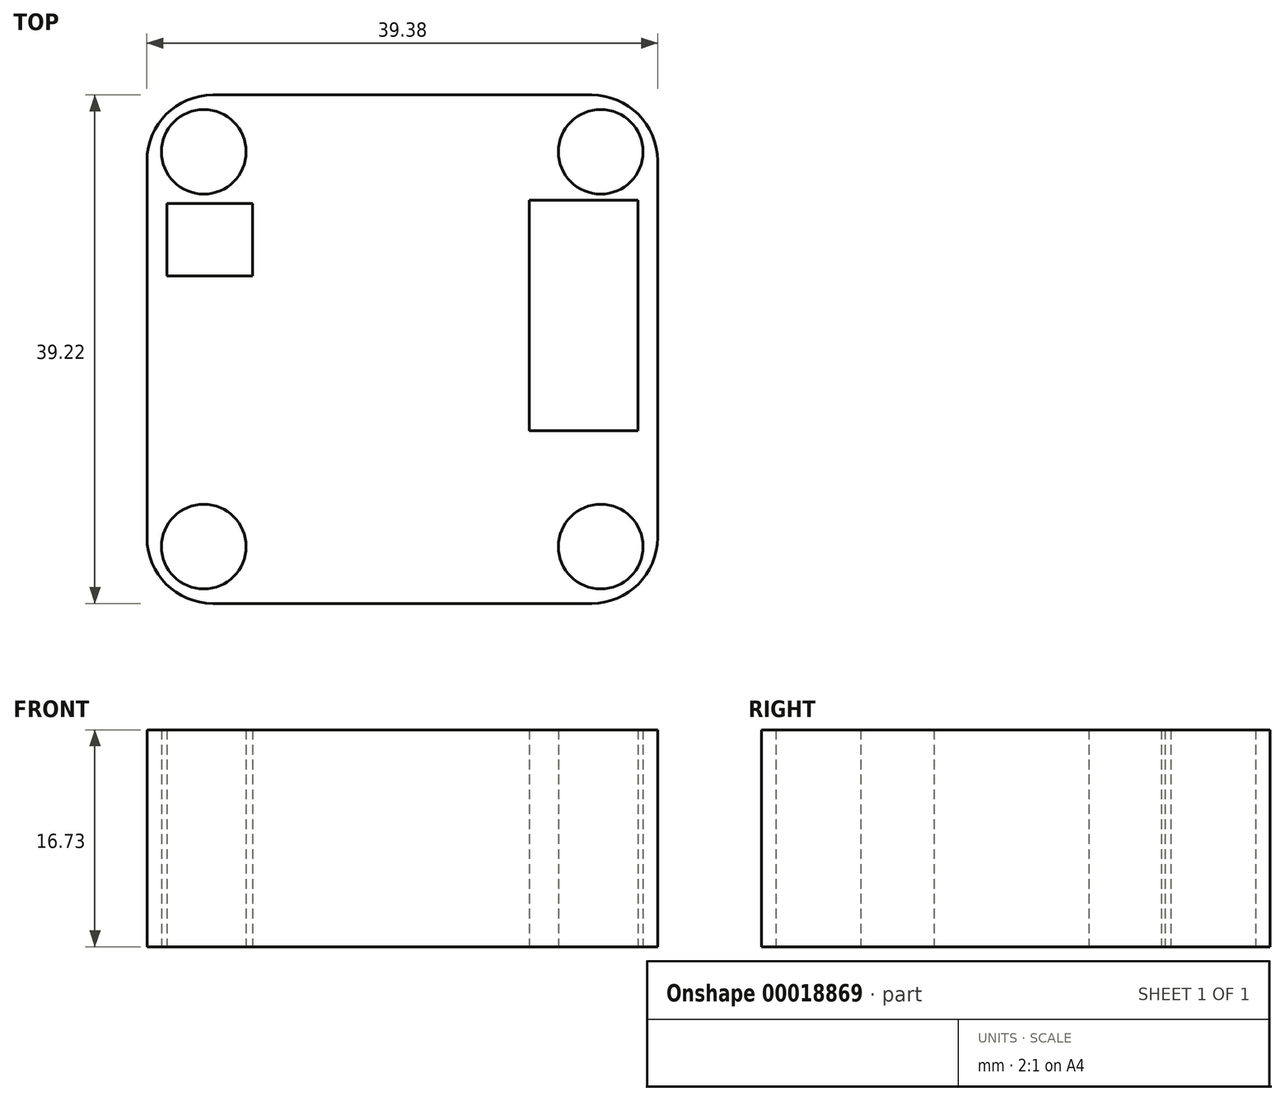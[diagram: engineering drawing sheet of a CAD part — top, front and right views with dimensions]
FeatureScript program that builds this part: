
annotation { "Feature Type Name" : "Feature", "Feature Type Description" : "" }
export const myFeature = defineFeature(function(context is Context, id is Id, definition is map)
    precondition{}
    {
        {
            var Q0;
            Q0=qCreatedBy(makeId("Top.planeOp"),FACE);
            var sketch = newSketch(context, id + "F0", { "sketchPlane" : qUnion([Q0])});
            skLineSegment(sketch, "E0.rect.bottom", {"start": v(19.69, -19.6) * mm, "end": v(-19.69, -19.6) * mm});
            skLineSegment(sketch, "E0.rect.top", {"start": v(19.69, 19.6) * mm, "end": v(-19.69, 19.6) * mm});
            skLineSegment(sketch, "E0.rect.left", {"start": v(19.69, -19.6) * mm, "end": v(19.69, 19.6) * mm});
            skLineSegment(sketch, "E0.rect.right", {"start": v(-19.69, -19.6) * mm, "end": v(-19.69, 19.6) * mm});
            skPoint(sketch, "E0.rect.middle", {"position": v(0, 0) * mm});
            skLineSegment(sketch, "E1.bottom", {"start": v(9.78, 11.5) * mm, "end": v(18.19, 11.5) * mm});
            skLineSegment(sketch, "E1.top", {"start": v(9.78, -6.3) * mm, "end": v(18.19, -6.3) * mm});
            skLineSegment(sketch, "E1.left", {"start": v(9.78, 11.5) * mm, "end": v(9.78, -6.3) * mm});
            skLineSegment(sketch, "E1.right", {"start": v(18.19, 11.5) * mm, "end": v(18.19, -6.3) * mm});
            skLineSegment(sketch, "E2.bottom", {"start": v(-18.16, 11.23) * mm, "end": v(-11.56, 11.23) * mm});
            skLineSegment(sketch, "E2.top", {"start": v(-18.16, 5.64) * mm, "end": v(-11.56, 5.64) * mm});
            skLineSegment(sketch, "E2.left", {"start": v(-18.16, 11.23) * mm, "end": v(-18.16, 5.64) * mm});
            skLineSegment(sketch, "E2.right", {"start": v(-11.56, 11.23) * mm, "end": v(-11.56, 5.64) * mm});
            skCircle(sketch, "E3", {"center": v(-15.3, -15.23) * mm, "radius": 3.26 * mm});
            skLineSegment(sketch, "E4", {"start": v(0, 0) * mm, "end": v(0, -19.6) * mm, "construction": true});
            skCircle(sketch, "E5.MirrorC", {"center": v(15.3, -15.23) * mm, "radius": 3.26 * mm});
            skLineSegment(sketch, "E6", {"start": v(0, 0) * mm, "end": v(-19.69, 0) * mm, "construction": true});
            skCircle(sketch, "E7.MirrorC", {"center": v(-15.3, 15.23) * mm, "radius": 3.26 * mm});
            skLineSegment(sketch, "E8", {"start": v(0, 0) * mm, "end": v(0, 19.6) * mm, "construction": true});
            skCircle(sketch, "E9.MirrorC", {"center": v(15.3, 15.23) * mm, "radius": 3.26 * mm});
            skSolve(sketch);
        }
        {
            var Q0;
            Q0=makeQuery(id+"F0.imprint","IMPRINT",FACE,{"disambiguationData":[TD([[makeQuery(id+"F0.imprint","IMPRINT",EDGE,{"derivedFrom":sQuery(id+"F0.wireOp",EDGE,"E0.rect.bottom")}),-1.0]])]});
            extrude(context, id + "F1", {"entities" : qUnion([Q0]), "depth" : 16.73 * mm});
        }
        {
            var Q0;
            Q0=makeQuery(id+"F1.opExtrude","SWEPT_EDGE",EDGE,{"disambiguationData":[OSD([sQuery(id+"F0.wireOp",EDGE,"E0.rect.top"),sQuery(id+"F0.wireOp",EDGE,"E0.rect.right")])]});
            var Q1;
            Q1=makeQuery(id+"F1.opExtrude","SWEPT_EDGE",EDGE,{"disambiguationData":[OSD([sQuery(id+"F0.wireOp",EDGE,"E0.rect.top"),sQuery(id+"F0.wireOp",EDGE,"E0.rect.left")])]});
            var Q2;
            Q2=makeQuery(id+"F1.opExtrude","SWEPT_EDGE",EDGE,{"disambiguationData":[OSD([sQuery(id+"F0.wireOp",EDGE,"E0.rect.bottom"),sQuery(id+"F0.wireOp",EDGE,"E0.rect.left")])]});
            var Q3;
            Q3=makeQuery(id+"F1.opExtrude","SWEPT_EDGE",EDGE,{"disambiguationData":[OSD([sQuery(id+"F0.wireOp",EDGE,"E0.rect.bottom"),sQuery(id+"F0.wireOp",EDGE,"E0.rect.right")])]});
            fillet(context, id + "F2", {"entities" : qUnion([Q0, Q1, Q2, Q3]), "radius" : 5.08 * mm, "tangentPropagation" : true, "allowEdgeOverflow" : false});
        }
    });
